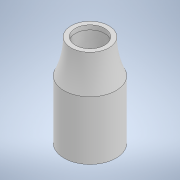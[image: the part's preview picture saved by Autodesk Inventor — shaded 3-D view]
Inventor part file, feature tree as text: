
AUTODESK INVENTOR PART (.ipt)
format: ipt  version: 2022 (Build 260153000, 153)  size: 158,720 bytes
history: native  units: mm
features: sketch x2, extrude x1, revolve x1
ambient origin geometry x8: Origin, YZ Plane, XZ Plane, XY Plane, X Axis, Y Axis, Z Axis, Center Point
bodies: Solid1 (feature_tree)
feature tree (4):
  extrude  "Extrusion1"  Depth=17.75mm
  revolve  "Revolution1"  [1 undecoded]
  sketch  "Sketch1"  dims[d0=15.0mm d1=17.75mm]
  sketch  "Sketch2"  dims[d2=20.0mm d3=0.0mm d4=5.0mm d5=10.0mm d6=0.0mm d8=1.5mm d9=90.0deg]
note: 1 required parameter value undecoded (feature->parameter linkage not recoverable at this tier; creation-order binding heuristic only, values carry confidence <= 0.55)
